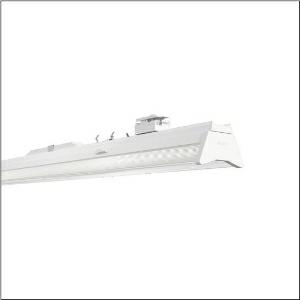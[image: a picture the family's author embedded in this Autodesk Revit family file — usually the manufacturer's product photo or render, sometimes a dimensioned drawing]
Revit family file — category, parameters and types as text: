
# Revit family: licross_r__21_performance_mo_52tm16cn49xg_ab5a
name_source: partatom
category: Lighting Fixtures
units: mm (PartAtom-declared; Revit-internal decimal feet)

## family parameters
Cut with Voids When Loaded = No
Host = Face
Light Source = No
Part Type = Normal
Room Calculation Point = No
Round Connector Dimension = Use Diameter
Shared = No

## types (1)
- --- (1 x LED, 9240 lm, 50.4 W, 4000K)
    Apparent Load = 50 VA
    CIE Flux Codes = 66 88 96 79 100
    Color Rendering = 80
    Color Temperature = 4000K
    Default Elevation = 1800 mm
    Description = Licross® 21 Performance MO, luminaire insert, of sheet steel, galvanised, coil coated, white, length: 1.500mm, width: 120mm, height: 123mm, LED rated luminous flux: 9.240lm, light colour: 840, control gear: ON/OFF Multilumen, CLOi, control gear: ECG Multilumen, with plug, 3-pole, with phase selection, mains connection: 220..240V, AC, 50/60Hz, halogen-free wiring, primary light control with lens, of plastic, primary optical cover: cover, of PMMA, light emission: direct/indirect distribution, primary light characteristic: symmetric, protection rating (complete): IP40, insulation class (complete): insulation class I (protective earthing), certification: CE, ENEC, UKCA, protection symbol: D if used in an environment without relevant dust loads with corresponding accessories, impact resistance: IK06, permissible ambient temperature for indoor applications: -35..+45°C, corresponds to IFS (International Featured Standards) requirements for safety and quality in the food industry, reducing of maximum allowable ambient temperature of 5°C with ceiling mounting, LABS conformity tested according to VDMA 24364:2018-05, packaging unit: 1 piece
    Height = 114 mm
    Lamp = 1 x LED
    Lamp Light Flux = 9240 lm
    Lamp Power = 50.4 W
    Lamp count = 1
    Length = 1500 mm
    Luminous efficacy = 183 lm/W
    Manufacturer = Siteco
    ModVariant = No
    Model = 52TM16CN49XG
    Mounting Place = Ceiling
    Mounting Type = Pendant
    Number of Poles = 1
    OnlyDefault = Yes
    Power Factor = 1
    Product Name = Licross® 21 Performance MO
    Product group = luminaire insert
    ProductGroupID = 902
    Protection Class = Protection class I
    Protection Degree = IP 40
    RLX_Detail_Level = 1
    RlxData = <blob elided: 31853 chars, md5=1a7931ba>
    Socket = socket
    Standby Power = 0 W
    System Light Flux = 9240 lm
    System Power = 50 W
    Type Comments = factory setting: luminous flux: 100 % | (A | C | E) | 117 mA
    Type Image = l_1256138.jpg
    URL = http://relux.com
    VarID = @adj_020017
    Voltage = 0 V
    Weight = 0.00 kg
    Width = 120 mm

## geometry (parser evidence)
native form markers: Blend x4, Sweep x11
no freeform markers — native parametric forms only
